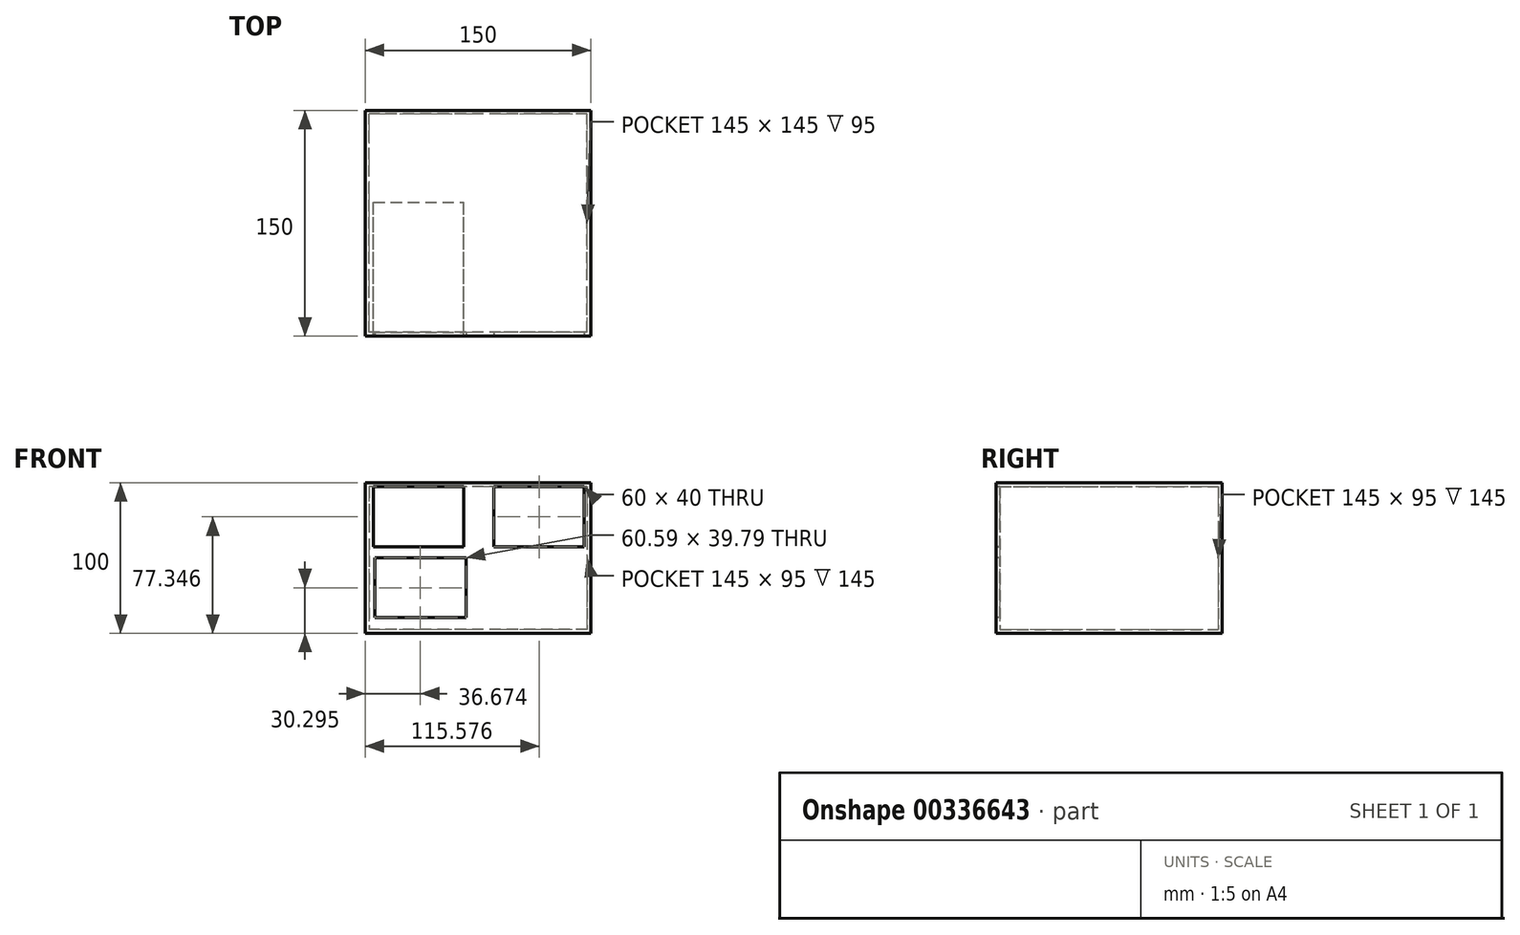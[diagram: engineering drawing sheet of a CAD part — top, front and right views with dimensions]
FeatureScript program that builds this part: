
annotation { "Feature Type Name" : "Feature", "Feature Type Description" : "" }
export const myFeature = defineFeature(function(context is Context, id is Id, definition is map)
    precondition{}
    {
        {
            var Q0;
            Q0=qCreatedBy(makeId("Right.planeOp"),FACE);
            var sketch = newSketch(context, id + "F0", { "sketchPlane" : qUnion([Q0])});
            skLineSegment(sketch, "E0.bottom", {"start": v(-88.78, 26.45) * mm, "end": v(61.22, 26.45) * mm});
            skLineSegment(sketch, "E0.top", {"start": v(-88.78, -73.55) * mm, "end": v(61.22, -73.55) * mm});
            skLineSegment(sketch, "E0.left", {"start": v(-88.78, 26.45) * mm, "end": v(-88.78, -73.55) * mm});
            skLineSegment(sketch, "E0.right", {"start": v(61.22, 26.45) * mm, "end": v(61.22, -73.55) * mm});
            skSolve(sketch);
        }
        {
            var Q0;
            Q0=qSketchRegion(id+"F0",true);
            extrude(context, id + "F1", {"entities" : qUnion([Q0]), "depth" : 150 * mm});
        }
        {
            var Q0;
            Q0=makeQuery(id+"F1.opExtrude","CAP_FACE",FACE,{"disambiguationData":[OSD([sQuery(id+"F0.wireOp",EDGE,"E0.bottom"),sQuery(id+"F0.wireOp",EDGE,"E0.top"),sQuery(id+"F0.wireOp",EDGE,"E0.left"),sQuery(id+"F0.wireOp",EDGE,"E0.right")])],"isStart":false});
            var Q1;
            Q1=makeQuery(id+"F1.opExtrude","CAP_FACE",FACE,{"disambiguationData":[OSD([sQuery(id+"F0.wireOp",EDGE,"E0.bottom"),sQuery(id+"F0.wireOp",EDGE,"E0.top"),sQuery(id+"F0.wireOp",EDGE,"E0.left"),sQuery(id+"F0.wireOp",EDGE,"E0.right")])],"isStart":true});
            var Q2;
            Q2=makeQuery(id+"F1.opExtrude","SWEPT_FACE",FACE,{"disambiguationData":[OSD([sQuery(id+"F0.wireOp",EDGE,"E0.bottom")])]});
            var Q3;
            Q3=makeQuery(id+"F1.opExtrude","SWEPT_FACE",FACE,{"disambiguationData":[OSD([sQuery(id+"F0.wireOp",EDGE,"E0.top")])]});
            var Q4;
            Q4=makeQuery(id+"F1.opExtrude","SWEPT_FACE",FACE,{"disambiguationData":[OSD([sQuery(id+"F0.wireOp",EDGE,"E0.left")])]});
            var Q5;
            Q5=makeQuery(id+"F1.opExtrude","SWEPT_FACE",FACE,{"disambiguationData":[OSD([sQuery(id+"F0.wireOp",EDGE,"E0.right")])]});
            var Q6;
            Q6=makeQuery(id+"F1.opExtrude","SWEPT_BODY",BODY,{"disambiguationData":[OSD([sQuery(id+"F0.wireOp",EDGE,"E0.bottom"),sQuery(id+"F0.wireOp",EDGE,"E0.top"),sQuery(id+"F0.wireOp",EDGE,"E0.left"),sQuery(id+"F0.wireOp",EDGE,"E0.right")])]});
            shell(context, id + "F2", {"isHollow" : true, "entities" : qUnion([Q0, Q1, Q2, Q3, Q4, Q5]), "parts" : qUnion([Q6]), "thickness" : 2.5 * mm});
        }
        {
            var Q0;
            Q0=qCreatedBy(makeId("Front.planeOp"),FACE);
            var sketch = newSketch(context, id + "F3", { "sketchPlane" : qUnion([Q0])});
            skLineSegment(sketch, "E1.bottom", {"start": v(5.42, 23.98) * mm, "end": v(65.42, 23.98) * mm});
            skLineSegment(sketch, "E1.top", {"start": v(5.42, -16.02) * mm, "end": v(65.42, -16.02) * mm});
            skLineSegment(sketch, "E1.left", {"start": v(5.42, 23.98) * mm, "end": v(5.42, -16.02) * mm});
            skLineSegment(sketch, "E1.right", {"start": v(65.42, 23.98) * mm, "end": v(65.42, -16.02) * mm});
            skSolve(sketch);
        }
        {
            var Q0;
            Q0=qSketchRegion(id+"F3",true);
            extrude(context, id + "F4", {"entities" : qUnion([Q0]), "operationType" : NewBodyOperationType.REMOVE, "depth" : 468.9 * mm});
        }
        {
            var Q0;
            Q0=makeQuery(id+"F1.opExtrude","SWEPT_FACE",FACE,{"disambiguationData":[OSD([sQuery(id+"F0.wireOp",EDGE,"E0.left")])]});
            var sketch = newSketch(context, id + "F5", { "sketchPlane" : qUnion([Q0])});
            skLineSegment(sketch, "E2.bottom", {"start": v(85.58, 23.8) * mm, "end": v(145.58, 23.8) * mm});
            skLineSegment(sketch, "E2.top", {"start": v(85.58, -16.2) * mm, "end": v(145.58, -16.2) * mm});
            skLineSegment(sketch, "E2.left", {"start": v(85.58, 23.8) * mm, "end": v(85.58, -16.2) * mm});
            skLineSegment(sketch, "E2.right", {"start": v(145.58, 23.8) * mm, "end": v(145.58, -16.2) * mm});
            skSolve(sketch);
        }
        {
            var Q0;
            Q0 = qSketchRegion(id + "F5", true);
            var Q1;
            Q1=makeQuery(id+"F5.imprint","IMPRINT",FACE,{"disambiguationData":[TD([[makeQuery(id+"F5.imprint","IMPRINT",EDGE,{"derivedFrom":sQuery(id+"F5.wireOp",EDGE,"E2.bottom")}),-1.0]])]});
            var Q2;
            Q2 = qSketchRegion(id + "F7", true);
            extrude(context, id + "F6", {"entities" : qUnion([Q0, Q1, Q2]), "operationType" : NewBodyOperationType.REMOVE, "oppositeDirection" : true, "depth" : 145 * mm});
        }
        {
            var Q0;
            Q0=makeQuery(id+"F5.imprint","IMPRINT",FACE,{"disambiguationData":[TD([[makeQuery(id+"F5.imprint","IMPRINT",EDGE,{"derivedFrom":sQuery(id+"F5.wireOp",EDGE,"E2.bottom")}),1.0]])]});
            var sketch = newSketch(context, id + "F7", { "sketchPlane" : qUnion([Q0])});
            skLineSegment(sketch, "E3.bottom", {"start": v(6.38, -23.36) * mm, "end": v(66.97, -23.36) * mm});
            skLineSegment(sketch, "E3.top", {"start": v(6.38, -63.15) * mm, "end": v(66.97, -63.15) * mm});
            skLineSegment(sketch, "E3.left", {"start": v(6.38, -23.36) * mm, "end": v(6.38, -63.15) * mm});
            skLineSegment(sketch, "E3.right", {"start": v(66.97, -23.36) * mm, "end": v(66.97, -63.15) * mm});
            skSolve(sketch);
        }
        {
            var Q0;
            Q0 = qSketchRegion(id + "F7", true);
            extrude(context, id + "F8", {"entities" : qUnion([Q0]), "operationType" : NewBodyOperationType.REMOVE, "oppositeDirection" : true, "depth" : 146.1 * mm});
        }
    });
